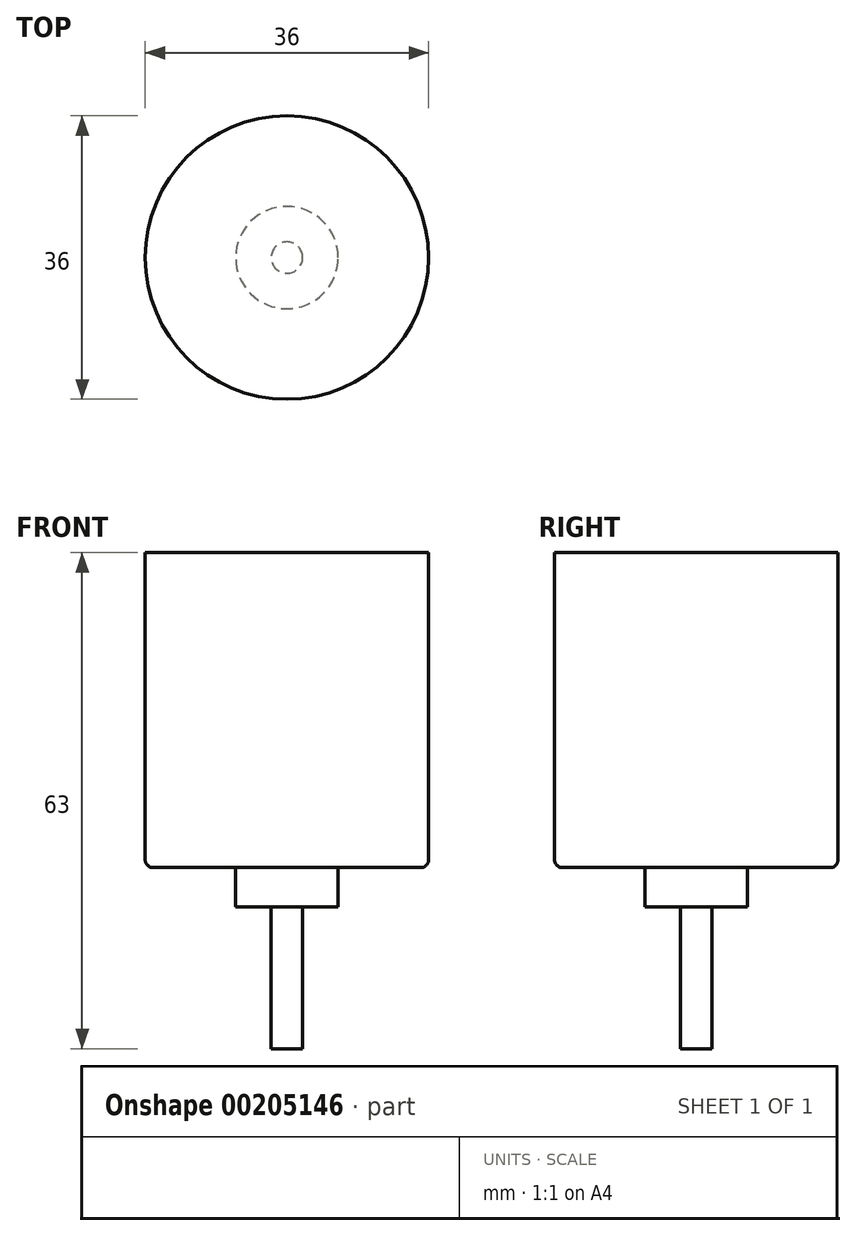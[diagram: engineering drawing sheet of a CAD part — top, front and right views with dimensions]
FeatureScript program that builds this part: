
annotation { "Feature Type Name" : "Feature", "Feature Type Description" : "" }
export const myFeature = defineFeature(function(context is Context, id is Id, definition is map)
    precondition{}
    {
        {
            var Q0;
            Q0=qCreatedBy(makeId("Top.planeOp"),FACE);
            var sketch = newSketch(context, id + "F0", { "sketchPlane" : qUnion([Q0])});
            skCircle(sketch, "E0", {"center": v(0, 0) * mm, "radius": 18 * mm});
            skSolve(sketch);
        }
        {
            var Q0;
            Q0=makeQuery(id+"F0.imprint","IMPRINT",FACE,{"disambiguationData":[TD([[makeQuery(id+"F0.imprint","IMPRINT",EDGE,{"derivedFrom":sQuery(id+"F0.wireOp",EDGE,"E0")}),1.0]])]});
            extrude(context, id + "F1", {"entities" : qUnion([Q0]), "depth" : 40 * mm});
        }
        {
            var Q0;
            Q0=qCreatedBy(makeId("Top.planeOp"),FACE);
            var sketch = newSketch(context, id + "F2", { "sketchPlane" : qUnion([Q0])});
            skCircle(sketch, "E1", {"center": v(0, 0) * mm, "radius": 6.5 * mm});
            skSolve(sketch);
        }
        {
            var Q0;
            Q0=makeQuery(id+"F2.imprint","IMPRINT",FACE,{"disambiguationData":[TD([[makeQuery(id+"F2.imprint","IMPRINT",EDGE,{"derivedFrom":sQuery(id+"F2.wireOp",EDGE,"E1")}),1.0]])]});
            extrude(context, id + "F3", {"entities" : qUnion([Q0]), "operationType" : NewBodyOperationType.ADD, "oppositeDirection" : true, "depth" : 5 * mm});
        }
        {
            var Q0;
            Q0=qCreatedBy(makeId("Top.planeOp"),FACE);
            var sketch = newSketch(context, id + "F4", { "sketchPlane" : qUnion([Q0])});
            skCircle(sketch, "E2", {"center": v(0, 0) * mm, "radius": 2 * mm});
            skSolve(sketch);
        }
        {
            var Q0;
            Q0 = qSketchRegion(id + "F4", true);
            extrude(context, id + "F5", {"entities" : qUnion([Q0]), "operationType" : NewBodyOperationType.ADD, "oppositeDirection" : true, "depth" : 23 * mm});
        }
        {
            var Q0;
            Q0=makeQuery(id+"F1.opExtrude","CAP_EDGE",EDGE,{"disambiguationData":[OSD([sQuery(id+"F0.wireOp",EDGE,"E0")])],"isStart":true});
            fillet(context, id + "F6", {"entities" : qUnion([Q0]), "radius" : 1 * mm, "tangentPropagation" : true, "allowEdgeOverflow" : false});
        }
    });
